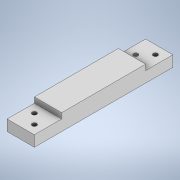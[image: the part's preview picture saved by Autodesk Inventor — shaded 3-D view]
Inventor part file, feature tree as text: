
AUTODESK INVENTOR PART (.ipt)
format: ipt  version: 2020 (Build 240168000, 168)  size: 131,584 bytes
history: native  units: mm
features: sketch x3, projected_geometry x3, extrude x2, other x1, hole x1
ambient origin geometry x8: Origin, YZ Plane, XZ Plane, XY Plane, X Axis, Y Axis, Z Axis, Center Point
bodies: Body1 (feature_tree)
feature tree (10):
  other  "솔리드1"
  extrude  "돌출1"  Depth=25.0mm
  extrude  "돌출2"  Depth=15.0mm
  hole  "구멍1"  [1 undecoded]
  sketch  "스케치1"
  sketch  "스케치2"
  projected_geometry  "투영된 루프1"
  sketch  "스케치3"
  projected_geometry  "투영된 루프2"
  projected_geometry  "투영된 루프3"
note: 1 required parameter value undecoded (feature->parameter linkage not recoverable at this tier; creation-order binding heuristic only, values carry confidence <= 0.55)
